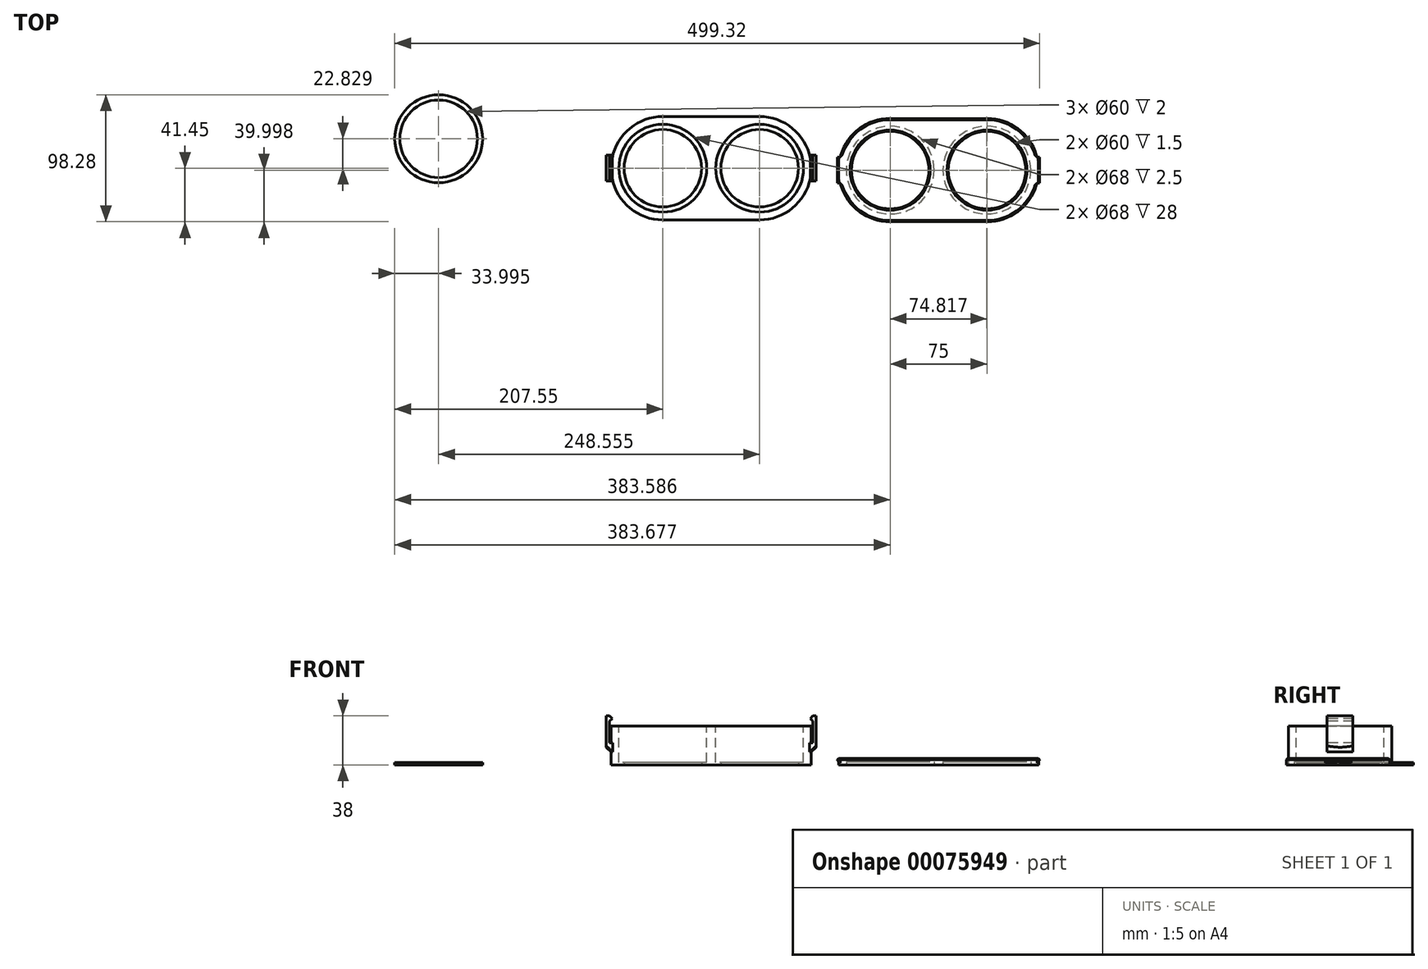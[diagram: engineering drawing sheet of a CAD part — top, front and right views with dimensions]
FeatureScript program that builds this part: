
annotation { "Feature Type Name" : "Feature", "Feature Type Description" : "" }
export const myFeature = defineFeature(function(context is Context, id is Id, definition is map)
    precondition{}
    {
        {
            var Q0;
            Q0=qCreatedBy(makeId("Top.planeOp"),FACE);
            var sketch = newSketch(context, id + "F0", { "sketchPlane" : qUnion([Q0])});
            skLineSegment(sketch, "E0", {"start": v(-37.5, 40) * mm, "end": v(37.5, 40) * mm});
            skLineSegment(sketch, "E1", {"start": v(-37.5, -40) * mm, "end": v(37.5, -40) * mm});
            skArc(sketch, "E2", {"start": v(-37.5, 40) * mm, "mid": v(-77.5, 0) * mm, "end": v(-37.5, -40) * mm});
            skArc(sketch, "E3", {"start": v(37.5, -40) * mm, "mid": v(77.5, 0) * mm, "end": v(37.5, 40) * mm});
            skCircle(sketch, "E4", {"center": v(-37.5, 0) * mm, "radius": 30 * mm});
            skCircle(sketch, "E5", {"center": v(37.5, 0) * mm, "radius": 30 * mm});
            skSolve(sketch);
        }
        {
            var Q0;
            Q0=qSketchRegion(id+"F0",true);
            extrude(context, id + "F1", {"entities" : qUnion([Q0]), "depth" : 30 * mm});
        }
        {
            var Q0;
            Q0=makeQuery(id+"F1.opExtrude","CAP_FACE",FACE,{"disambiguationData":[OSD([sQuery(id+"F0.wireOp",EDGE,"E0"),sQuery(id+"F0.wireOp",EDGE,"E1"),sQuery(id+"F0.wireOp",EDGE,"E2"),sQuery(id+"F0.wireOp",EDGE,"E3"),sQuery(id+"F0.wireOp",EDGE,"E4"),sQuery(id+"F0.wireOp",EDGE,"E5")])],"isStart":false});
            var sketch = newSketch(context, id + "F2", { "sketchPlane" : qUnion([Q0])});
            skCircle(sketch, "E6", {"center": v(-37.5, 0) * mm, "radius": 34 * mm});
            skCircle(sketch, "E7", {"center": v(37.5, 0) * mm, "radius": 34 * mm});
            skSolve(sketch);
        }
        {
            var Q0;
            Q0=qSketchRegion(id+"F2",true);
            extrude(context, id + "F3", {"entities" : qUnion([Q0]), "operationType" : NewBodyOperationType.REMOVE, "oppositeDirection" : true, "depth" : 28 * mm});
        }
        {
            var Q0;
            Q0=qCreatedBy(makeId("Top.planeOp"),FACE);
            var sketch = newSketch(context, id + "F4", { "sketchPlane" : qUnion([Q0])});
            skCircle(sketch, "E8", {"center": v(-211.05, 22.83) * mm, "radius": 30 * mm});
            skCircle(sketch, "E9", {"center": v(-211.05, 22.83) * mm, "radius": 34 * mm});
            skSolve(sketch);
        }
        {
            var Q0;
            Q0=qSketchRegion(id+"F4",true);
            extrude(context, id + "F5", {"entities" : qUnion([Q0]), "depth" : 2 * mm});
        }
        {
            var Q0;
            Q0=qCreatedBy(makeId("Top.planeOp"),FACE);
            var sketch = newSketch(context, id + "F6", { "sketchPlane" : qUnion([Q0])});
            skLineSegment(sketch, "E10", {"start": v(138.54, 38.55) * mm, "end": v(213.54, 38.55) * mm});
            skLineSegment(sketch, "E11", {"start": v(138.54, -41.45) * mm, "end": v(213.54, -41.45) * mm});
            skArc(sketch, "E12", {"start": v(138.54, 38.55) * mm, "mid": v(98.54, -1.45) * mm, "end": v(138.54, -41.45) * mm});
            skArc(sketch, "E13", {"start": v(213.54, -41.45) * mm, "mid": v(253.54, -1.45) * mm, "end": v(213.54, 38.55) * mm});
            skCircle(sketch, "E14", {"center": v(138.54, -1.45) * mm, "radius": 30 * mm});
            skCircle(sketch, "E15", {"center": v(213.54, -1.45) * mm, "radius": 30 * mm});
            skLineSegment(sketch, "E16", {"start": v(176.04, -41.45) * mm, "end": v(176.04, 38.55) * mm, "construction": true});
            skSolve(sketch);
        }
        {
            var Q0;
            Q0=qSketchRegion(id+"F6",true);
            extrude(context, id + "F7", {"entities" : qUnion([Q0]), "depth" : 5 * mm});
        }
        {
            var Q0;
            Q0=makeQuery(id+"F7.opExtrude","CAP_FACE",FACE,{"disambiguationData":[OSD([sQuery(id+"F6.wireOp",EDGE,"E10"),sQuery(id+"F6.wireOp",EDGE,"E11"),sQuery(id+"F6.wireOp",EDGE,"E12"),sQuery(id+"F6.wireOp",EDGE,"E13"),sQuery(id+"F6.wireOp",EDGE,"E14"),sQuery(id+"F6.wireOp",EDGE,"E15")])],"isStart":true});
            var sketch = newSketch(context, id + "F8", { "sketchPlane" : qUnion([Q0])});
            skCircle(sketch, "E17", {"center": v(138.63, 1.45) * mm, "radius": 34 * mm});
            skCircle(sketch, "E18", {"center": v(213.44, 1.45) * mm, "radius": 34 * mm});
            skSolve(sketch);
        }
        {
            var Q0;
            Q0=qSketchRegion(id+"F8",true);
            extrude(context, id + "F9", {"entities" : qUnion([Q0]), "operationType" : NewBodyOperationType.REMOVE, "oppositeDirection" : true, "depth" : 2.5 * mm});
        }
        {
            var Q0;
            Q0=qCreatedBy(makeId("Top.planeOp"),FACE);
            cPlane(context, id + "F10", {"entities" : qUnion([Q0]), "cplaneType" : CPlaneType.OFFSET, "offset" : 15 * mm, "width" : 150 * mm, "height" : 150 * mm});
        }
        {
            var Q0;
            Q0=qCreatedBy(id+"F10.planeOp",FACE);
            var sketch = newSketch(context, id + "F11", { "sketchPlane" : qUnion([Q0])});
            skLineSegment(sketch, "E19.bottom", {"start": v(-81.23, 10) * mm, "end": v(-76.23, 10) * mm});
            skLineSegment(sketch, "E19.top", {"start": v(-81.23, -10) * mm, "end": v(-76.23, -10) * mm});
            skLineSegment(sketch, "E19.left", {"start": v(-81.23, 10) * mm, "end": v(-81.23, -10) * mm});
            skLineSegment(sketch, "E19.right", {"start": v(-76.23, 10) * mm, "end": v(-76.23, -10) * mm});
            skPoint(sketch, "E19.middle", {"position": v(-78.73, 0) * mm});
            skLineSegment(sketch, "E20.MirrorCS", {"start": v(81.23, -10) * mm, "end": v(76.23, -10) * mm});
            skLineSegment(sketch, "E21.MirrorCS", {"start": v(81.23, 10) * mm, "end": v(76.23, 10) * mm});
            skPoint(sketch, "E22.MirrorP", {"position": v(78.73, 0) * mm});
            skLineSegment(sketch, "E23.MirrorCS", {"start": v(81.23, 10) * mm, "end": v(81.23, -10) * mm});
            skLineSegment(sketch, "E24.MirrorCS", {"start": v(76.23, 10) * mm, "end": v(76.23, -10) * mm});
            skSolve(sketch);
        }
        {
            var Q0;
            Q0 = qSketchRegion(id + "F11", true);
            extrude(context, id + "F12", {"entities" : qUnion([Q0]), "operationType" : NewBodyOperationType.ADD, "depth" : 2 * mm});
        }
        {
            var Q0;
            Q0=makeQuery(id+"F12.opExtrude","CAP_FACE",FACE,{"disambiguationData":[OSD([sQuery(id+"F11.wireOp",EDGE,"E19.bottom"),sQuery(id+"F11.wireOp",EDGE,"E19.top"),sQuery(id+"F11.wireOp",EDGE,"E19.left"),sQuery(id+"F11.wireOp",EDGE,"E19.right")])],"isStart":false});
            var sketch = newSketch(context, id + "F13", { "sketchPlane" : qUnion([Q0])});
            skLineSegment(sketch, "E25.bottom", {"start": v(-81.23, 10) * mm, "end": v(-78.73, 10) * mm});
            skLineSegment(sketch, "E25.top", {"start": v(-81.23, -10) * mm, "end": v(-78.73, -10) * mm});
            skLineSegment(sketch, "E25.left", {"start": v(-81.23, 10) * mm, "end": v(-81.23, -10) * mm});
            skLineSegment(sketch, "E25.right", {"start": v(-78.73, 10) * mm, "end": v(-78.73, -10) * mm});
            skLineSegment(sketch, "E26.MirrorCS", {"start": v(81.23, 10) * mm, "end": v(78.73, 10) * mm});
            skLineSegment(sketch, "E27.MirrorCS", {"start": v(81.23, -10) * mm, "end": v(78.73, -10) * mm});
            skLineSegment(sketch, "E28.MirrorCS", {"start": v(78.73, 10) * mm, "end": v(78.73, -10) * mm});
            skLineSegment(sketch, "E29.MirrorCS", {"start": v(81.23, 10) * mm, "end": v(81.23, -10) * mm});
            skSolve(sketch);
        }
        {
            var Q0;
            Q0 = qSketchRegion(id + "F13", true);
            extrude(context, id + "F14", {"entities" : qUnion([Q0]), "operationType" : NewBodyOperationType.ADD, "depth" : 21 * mm});
        }
        {
            var Q0;
            Q0=makeQuery(id+"F14.boolean.opBoolean","MERGE",FACE,{"derivedFrom":[makeQuery(id+"F12.opExtrude","SWEPT_FACE",FACE,{"disambiguationData":[OSD([sQuery(id+"F11.wireOp",EDGE,"E19.top")])]}),makeQuery(id+"F14.opExtrude","SWEPT_FACE",FACE,{"disambiguationData":[OSD([sQuery(id+"F13.wireOp",EDGE,"E25.top")])]})]});
            var sketch = newSketch(context, id + "F15", { "sketchPlane" : qUnion([Q0])});
            skLineSegment(sketch, "E30", {"start": v(-78.73, 38) * mm, "end": v(-76.73, 36) * mm});
            skLineSegment(sketch, "E31", {"start": v(-76.73, 36) * mm, "end": v(-78.73, 34) * mm});
            skLineSegment(sketch, "E32", {"start": v(-78.73, 34) * mm, "end": v(-78.73, 38) * mm});
            skLineSegment(sketch, "E33.MirrorCS", {"start": v(76.73, 36) * mm, "end": v(78.73, 34) * mm});
            skLineSegment(sketch, "E34.MirrorCS", {"start": v(78.73, 38) * mm, "end": v(76.73, 36) * mm});
            skLineSegment(sketch, "E35.MirrorCS", {"start": v(78.73, 34) * mm, "end": v(78.73, 38) * mm});
            skSolve(sketch);
        }
        {
            var Q0;
            Q0 = qSketchRegion(id + "F15", true);
            var Q1;
            Q1=makeQuery(id+"F14.boolean.opBoolean","MERGE",FACE,{"derivedFrom":[makeQuery(id+"F12.opExtrude","SWEPT_FACE",FACE,{"disambiguationData":[OSD([sQuery(id+"F11.wireOp",EDGE,"E19.bottom")])]}),makeQuery(id+"F14.opExtrude","SWEPT_FACE",FACE,{"disambiguationData":[OSD([sQuery(id+"F13.wireOp",EDGE,"E25.bottom")])]})]});
            extrude(context, id + "F16", {"entities" : qUnion([Q0]), "operationType" : NewBodyOperationType.ADD, "endBound" : BoundingType.UP_TO_SURFACE, "oppositeDirection" : true, "endBoundEntityFace" : qUnion([Q1]), "depth" : 25 * mm});
        }
        {
            var Q0;
            Q0=makeQuery(id+"F7.opExtrude","CAP_FACE",FACE,{"disambiguationData":[OSD([sQuery(id+"F6.wireOp",EDGE,"E10"),sQuery(id+"F6.wireOp",EDGE,"E11"),sQuery(id+"F6.wireOp",EDGE,"E12"),sQuery(id+"F6.wireOp",EDGE,"E13"),sQuery(id+"F6.wireOp",EDGE,"E14"),sQuery(id+"F6.wireOp",EDGE,"E15")])],"isStart":false});
            var sketch = newSketch(context, id + "F17", { "sketchPlane" : qUnion([Q0])});
            skLineSegment(sketch, "E36.bottom", {"start": v(97.8, 8.55) * mm, "end": v(99.8, 8.55) * mm});
            skLineSegment(sketch, "E36.top", {"start": v(97.8, -11.45) * mm, "end": v(99.8, -11.45) * mm});
            skLineSegment(sketch, "E36.left", {"start": v(97.8, 8.55) * mm, "end": v(97.8, -11.45) * mm});
            skLineSegment(sketch, "E36.right", {"start": v(99.8, 8.55) * mm, "end": v(99.8, -11.45) * mm});
            skLineSegment(sketch, "E37", {"start": v(176.04, 38.55) * mm, "end": v(176.04, -41.45) * mm, "construction": true});
            skLineSegment(sketch, "E38", {"start": v(176.04, -1.45) * mm, "end": v(176.04, -1.45) * mm});
            skPoint(sketch, "E38.endSnap0", {"position": v(98.54, -1.45) * mm});
            skPoint(sketch, "E39", {"position": v(99.8, -1.45) * mm});
            skLineSegment(sketch, "E40.MirrorCS", {"start": v(254.27, 8.55) * mm, "end": v(252.27, 8.55) * mm});
            skLineSegment(sketch, "E41.MirrorCS", {"start": v(254.27, -11.45) * mm, "end": v(252.27, -11.45) * mm});
            skLineSegment(sketch, "E42.MirrorCS", {"start": v(254.27, 8.55) * mm, "end": v(254.27, -11.45) * mm});
            skPoint(sketch, "E43.MirrorP", {"position": v(253.54, -1.45) * mm});
            skPoint(sketch, "E44.MirrorP", {"position": v(252.27, -1.45) * mm});
            skLineSegment(sketch, "E45.MirrorCS", {"start": v(252.27, 8.55) * mm, "end": v(252.27, -11.45) * mm});
            skSolve(sketch);
        }
        {
            var Q0;
            Q0 = qSketchRegion(id + "F17", true);
            extrude(context, id + "F18", {"entities" : qUnion([Q0]), "operationType" : NewBodyOperationType.ADD, "oppositeDirection" : true, "depth" : 2 * mm});
        }
        {
            var Q0;
            Q0=makeQuery(id+"F18.opExtrude","CAP_EDGE",EDGE,{"disambiguationData":[OSD([sQuery(id+"F17.wireOp",EDGE,"E36.left")])],"isStart":false});
            var Q1;
            Q1=makeQuery(id+"F18.opExtrude","CAP_EDGE",EDGE,{"disambiguationData":[OSD([sQuery(id+"F17.wireOp",EDGE,"E42.MirrorCS")])],"isStart":false});
            chamfer(context, id + "F19", {"entities" : qUnion([Q0, Q1]), "width" : .6 * mm, "tangentPropagation" : true});
        }
        {
            var Q0;
            Q0=makeQuery(id+"F7.opExtrude","CAP_EDGE",EDGE,{"disambiguationData":[OSD([sQuery(id+"F6.wireOp",EDGE,"E14")])],"isStart":false});
            var Q1;
            Q1=makeQuery(id+"F7.opExtrude","CAP_EDGE",EDGE,{"disambiguationData":[OSD([sQuery(id+"F6.wireOp",EDGE,"E15")])],"isStart":false});
            var Q2;
            Q2=makeQuery(id+"F7.opExtrude","CAP_EDGE",EDGE,{"disambiguationData":[OSD([sQuery(id+"F6.wireOp",EDGE,"E11")])],"isStart":false});
            var Q3;
            Q3=makeQuery(id+"F7.opExtrude","CAP_EDGE",EDGE,{"disambiguationData":[OSD([sQuery(id+"F6.wireOp",EDGE,"E10")])],"isStart":false});
            chamfer(context, id + "F20", {"entities" : qUnion([Q0, Q1, Q2, Q3]), "width" : 1 * mm, "tangentPropagation" : true});
        }
        {
            var Q0;
            Q0=makeQuery(id+"F18.boolean.opBoolean","INTERSECT",EDGE,{"derivedFrom":[makeQuery(id+"F7.opExtrude","SWEPT_FACE",FACE,{"disambiguationData":[OSD([sQuery(id+"F6.wireOp",EDGE,"E12")])]}),makeQuery(id+"F18.opExtrude","CAP_FACE",FACE,{"disambiguationData":[OSD([sQuery(id+"F17.wireOp",EDGE,"E36.bottom"),sQuery(id+"F17.wireOp",EDGE,"E36.top"),sQuery(id+"F17.wireOp",EDGE,"E36.left"),sQuery(id+"F17.wireOp",EDGE,"E36.right")])],"isStart":false})]});
            var Q1;
            Q1=makeQuery(id+"F18.boolean.opBoolean","INTERSECT",EDGE,{"derivedFrom":[makeQuery(id+"F7.opExtrude","SWEPT_FACE",FACE,{"disambiguationData":[OSD([sQuery(id+"F6.wireOp",EDGE,"E13")])]}),makeQuery(id+"F18.opExtrude","CAP_FACE",FACE,{"disambiguationData":[OSD([sQuery(id+"F17.wireOp",EDGE,"E40.MirrorCS"),sQuery(id+"F17.wireOp",EDGE,"E41.MirrorCS"),sQuery(id+"F17.wireOp",EDGE,"E42.MirrorCS"),sQuery(id+"F17.wireOp",EDGE,"E45.MirrorCS")])],"isStart":false})]});
            fillet(context, id + "F21", {"entities" : qUnion([Q0, Q1]), "radius" : 1.6 * mm, "tangentPropagation" : true, "allowEdgeOverflow" : false});
        }
        {
            var Q0;
            Q0=makeQuery(id+"F18.opExtrude","SWEPT_EDGE",EDGE,{"disambiguationData":[OSD([sQuery(id+"F6.wireOp",EDGE,"E12"),sQuery(id+"F17.wireOp",EDGE,"E36.bottom"),sQuery(id+"F17.wireOp",EDGE,"E36.right")])]});
            var Q1;
            {var subQ0=sQuery(id+"F17.wireOp",EDGE,"E36.bottom");var subQ1=makeQuery(id+"F18.opExtrude","SWEPT_FACE",FACE,{"disambiguationData":[OSD([subQ0])]});var subQ2=sQuery(id+"F6.wireOp",EDGE,"E12");var subQ3=sQuery(id+"F6.wireOp",EDGE,"E10");Q1=makeQuery(id+"F20.opChamfer","BLEND_EDGE",EDGE,{"blendedFrom":[makeQuery(id+"F18.boolean.opBoolean","SPLIT",EDGE,{"disambiguationData":[TD([makeQuery(id+"F7.opExtrude","SWEPT_FACE",FACE,{"disambiguationData":[OSD([subQ3])]})])],"derivedFrom":makeQuery(id+"F7.opExtrude","CAP_EDGE",EDGE,{"disambiguationData":[OSD([subQ2])],"isStart":false})}),subQ1],"blendedInto":[subQ1]});}
            var Q2;
            Q2=makeQuery(id+"F18.opExtrude","SWEPT_EDGE",EDGE,{"disambiguationData":[OSD([sQuery(id+"F6.wireOp",EDGE,"E12"),sQuery(id+"F17.wireOp",EDGE,"E36.top"),sQuery(id+"F17.wireOp",EDGE,"E36.right")])]});
            var Q3;
            {var subQ0=sQuery(id+"F17.wireOp",EDGE,"E36.top");var subQ1=makeQuery(id+"F18.opExtrude","SWEPT_FACE",FACE,{"disambiguationData":[OSD([subQ0])]});var subQ2=sQuery(id+"F6.wireOp",EDGE,"E12");var subQ3=sQuery(id+"F6.wireOp",EDGE,"E11");Q3=makeQuery(id+"F20.opChamfer","BLEND_EDGE",EDGE,{"blendedFrom":[makeQuery(id+"F18.boolean.opBoolean","SPLIT",EDGE,{"disambiguationData":[TD([makeQuery(id+"F7.opExtrude","SWEPT_FACE",FACE,{"disambiguationData":[OSD([subQ3])]})])],"derivedFrom":makeQuery(id+"F7.opExtrude","CAP_EDGE",EDGE,{"disambiguationData":[OSD([subQ2])],"isStart":false})}),subQ1],"blendedInto":[subQ1]});}
            var Q4;
            Q4=makeQuery(id+"F18.opExtrude","SWEPT_EDGE",EDGE,{"disambiguationData":[OSD([sQuery(id+"F6.wireOp",EDGE,"E13"),sQuery(id+"F17.wireOp",EDGE,"E41.MirrorCS"),sQuery(id+"F17.wireOp",EDGE,"E45.MirrorCS")])]});
            var Q5;
            {var subQ0=sQuery(id+"F17.wireOp",EDGE,"E41.MirrorCS");var subQ1=makeQuery(id+"F18.opExtrude","SWEPT_FACE",FACE,{"disambiguationData":[OSD([subQ0])]});var subQ2=sQuery(id+"F6.wireOp",EDGE,"E13");var subQ3=sQuery(id+"F6.wireOp",EDGE,"E11");Q5=makeQuery(id+"F20.opChamfer","BLEND_EDGE",EDGE,{"blendedFrom":[makeQuery(id+"F18.boolean.opBoolean","SPLIT",EDGE,{"disambiguationData":[TD([makeQuery(id+"F7.opExtrude","SWEPT_FACE",FACE,{"disambiguationData":[OSD([subQ3])]})])],"derivedFrom":makeQuery(id+"F7.opExtrude","CAP_EDGE",EDGE,{"disambiguationData":[OSD([subQ2])],"isStart":false})}),subQ1],"blendedInto":[subQ1]});}
            var Q6;
            {var subQ0=sQuery(id+"F17.wireOp",EDGE,"E40.MirrorCS");var subQ1=makeQuery(id+"F18.opExtrude","SWEPT_FACE",FACE,{"disambiguationData":[OSD([subQ0])]});var subQ2=sQuery(id+"F6.wireOp",EDGE,"E13");var subQ3=sQuery(id+"F6.wireOp",EDGE,"E10");Q6=makeQuery(id+"F20.opChamfer","BLEND_EDGE",EDGE,{"blendedFrom":[makeQuery(id+"F18.boolean.opBoolean","SPLIT",EDGE,{"disambiguationData":[TD([makeQuery(id+"F7.opExtrude","SWEPT_FACE",FACE,{"disambiguationData":[OSD([subQ3])]})])],"derivedFrom":makeQuery(id+"F7.opExtrude","CAP_EDGE",EDGE,{"disambiguationData":[OSD([subQ2])],"isStart":false})}),subQ1],"blendedInto":[subQ1]});}
            var Q7;
            Q7=makeQuery(id+"F18.opExtrude","SWEPT_EDGE",EDGE,{"disambiguationData":[OSD([sQuery(id+"F6.wireOp",EDGE,"E13"),sQuery(id+"F17.wireOp",EDGE,"E40.MirrorCS"),sQuery(id+"F17.wireOp",EDGE,"E45.MirrorCS")])]});
            fillet(context, id + "F22", {"entities" : qUnion([Q0, Q1, Q2, Q3, Q4, Q5, Q6, Q7]), "radius" : 2.2 * mm, "tangentPropagation" : true, "allowEdgeOverflow" : false});
        }
        {
            var Q0;
            Q0=makeQuery(id+"F12.boolean.opBoolean","INTERSECT",EDGE,{"derivedFrom":[makeQuery(id+"F1.opExtrude","SWEPT_FACE",FACE,{"disambiguationData":[OSD([sQuery(id+"F0.wireOp",EDGE,"E3")])]}),makeQuery(id+"F12.opExtrude","CAP_FACE",FACE,{"disambiguationData":[OSD([sQuery(id+"F11.wireOp",EDGE,"E20.MirrorCS"),sQuery(id+"F11.wireOp",EDGE,"E21.MirrorCS"),sQuery(id+"F11.wireOp",EDGE,"E23.MirrorCS"),sQuery(id+"F11.wireOp",EDGE,"E24.MirrorCS")])],"isStart":true})]});
            var Q1;
            Q1=makeQuery(id+"F12.boolean.opBoolean","INTERSECT",EDGE,{"derivedFrom":[makeQuery(id+"F1.opExtrude","SWEPT_FACE",FACE,{"disambiguationData":[OSD([sQuery(id+"F0.wireOp",EDGE,"E2")])]}),makeQuery(id+"F12.opExtrude","CAP_FACE",FACE,{"disambiguationData":[OSD([sQuery(id+"F11.wireOp",EDGE,"E19.bottom"),sQuery(id+"F11.wireOp",EDGE,"E19.top"),sQuery(id+"F11.wireOp",EDGE,"E19.left"),sQuery(id+"F11.wireOp",EDGE,"E19.right")])],"isStart":true})]});
            chamfer(context, id + "F23", {"entities" : qUnion([Q0, Q1]), "width" : 5 * mm, "tangentPropagation" : true});
        }
        {
            var Q0;
            Q0=makeQuery(id+"F18.opExtrude","CAP_EDGE",EDGE,{"disambiguationData":[OSD([sQuery(id+"F17.wireOp",EDGE,"E42.MirrorCS")])],"isStart":true});
            var Q1;
            Q1=makeQuery(id+"F18.opExtrude","CAP_EDGE",EDGE,{"disambiguationData":[OSD([sQuery(id+"F17.wireOp",EDGE,"E36.left")])],"isStart":true});
            chamfer(context, id + "F24", {"entities" : qUnion([Q0, Q1]), "width" : 1 * mm, "tangentPropagation" : true});
        }
    });
